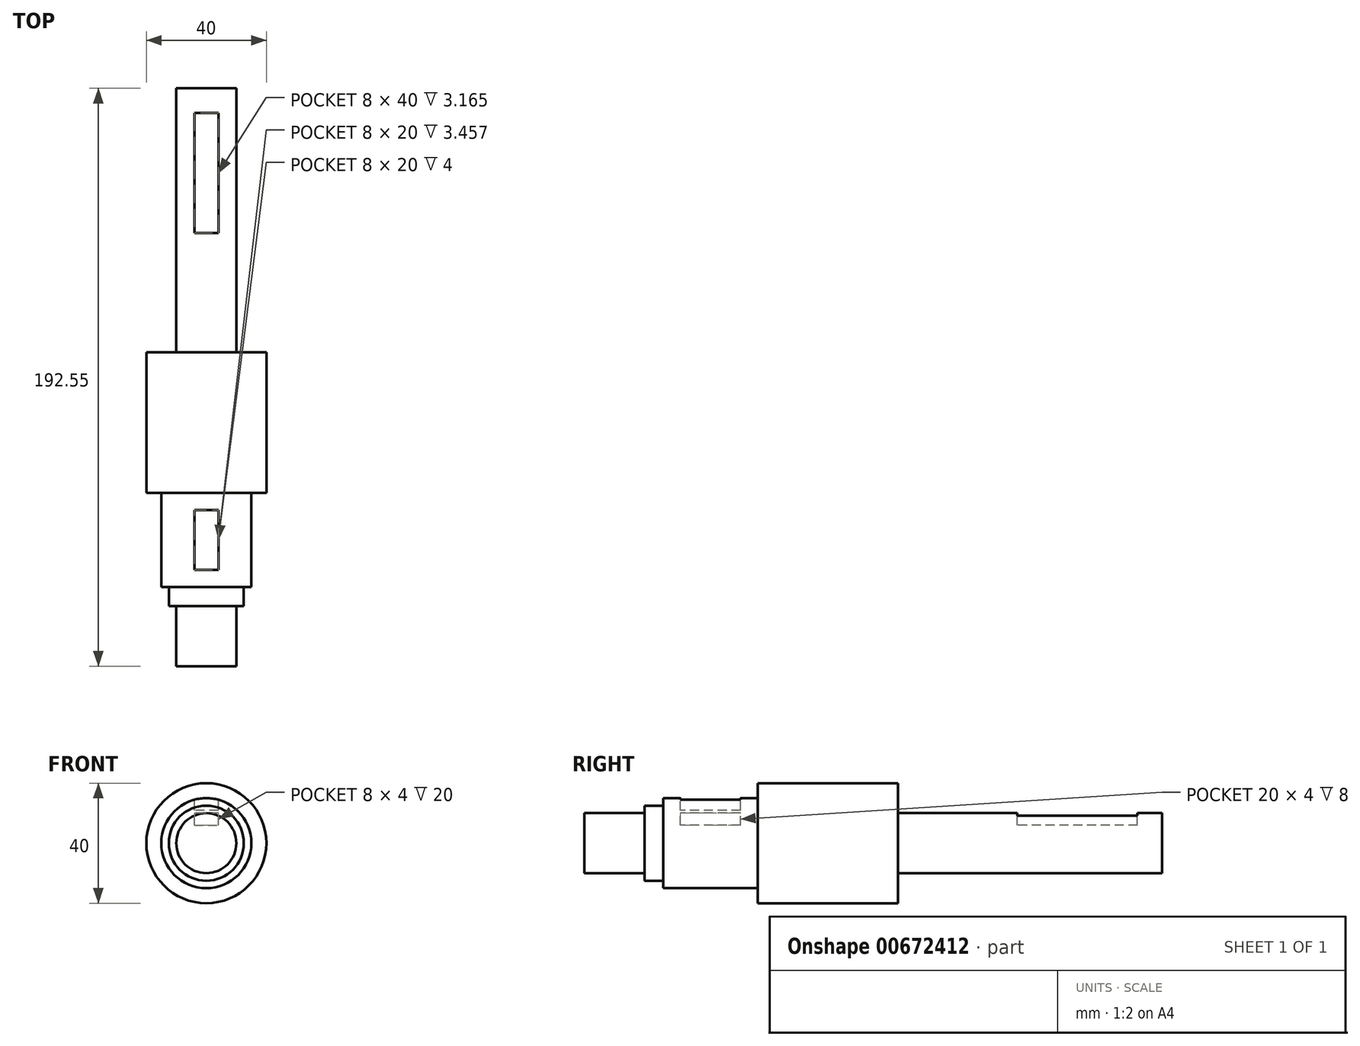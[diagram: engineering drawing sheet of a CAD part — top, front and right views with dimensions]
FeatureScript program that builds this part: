
annotation { "Feature Type Name" : "Feature", "Feature Type Description" : "" }
export const myFeature = defineFeature(function(context is Context, id is Id, definition is map)
    precondition{}
    {
        {
            var Q0;
            Q0=qCreatedBy(makeId("Front.planeOp"),FACE);
            var sketch = newSketch(context, id + "F0", { "sketchPlane" : qUnion([Q0])});
            skCircle(sketch, "E0", {"center": v(0, 0) * mm, "radius": 10 * mm});
            skSolve(sketch);
        }
        {
            var Q0;
            Q0 = qSketchRegion(id + "F0", true);
            extrude(context, id + "F1", {"entities" : qUnion([Q0]), "depth" : 88 * mm, "offsetDistance" : 25.4 * mm});
        }
        {
            var Q0;
            Q0=makeQuery(id+"F1.opExtrude","CAP_FACE",FACE,{"disambiguationData":[OSD([sQuery(id+"F0.wireOp",EDGE,"E0")])],"isStart":false});
            var sketch = newSketch(context, id + "F2", { "sketchPlane" : qUnion([Q0])});
            skCircle(sketch, "E1", {"center": v(0, 0) * mm, "radius": 20 * mm});
            skSolve(sketch);
        }
        {
            var Q0;
            Q0 = qSketchRegion(id + "F2", true);
            extrude(context, id + "F3", {"entities" : qUnion([Q0]), "operationType" : NewBodyOperationType.ADD, "depth" : 46.83 * mm, "offsetDistance" : 25.4 * mm});
        }
        {
            var Q0;
            Q0=makeQuery(id+"F3.opExtrude","CAP_FACE",FACE,{"disambiguationData":[OSD([sQuery(id+"F2.wireOp",EDGE,"E1")])],"isStart":false});
            var sketch = newSketch(context, id + "F4", { "sketchPlane" : qUnion([Q0])});
            skCircle(sketch, "E2", {"center": v(0, 0) * mm, "radius": 15 * mm});
            skSolve(sketch);
        }
        {
            var Q0;
            Q0 = qSketchRegion(id + "F4", true);
            extrude(context, id + "F5", {"entities" : qUnion([Q0]), "operationType" : NewBodyOperationType.ADD, "depth" : 25.4 * mm + 6 * mm, "offsetDistance" : 25.4 * mm});
        }
        {
            var Q0;
            Q0=makeQuery(id+"F5.opExtrude","CAP_FACE",FACE,{"disambiguationData":[OSD([sQuery(id+"F4.wireOp",EDGE,"E2")])],"isStart":false});
            var sketch = newSketch(context, id + "F6", { "sketchPlane" : qUnion([Q0])});
            skCircle(sketch, "E3", {"center": v(0, 0) * mm, "radius": 12.5 * mm});
            skSolve(sketch);
        }
        {
            var Q0;
            Q0 = qSketchRegion(id + "F6", true);
            extrude(context, id + "F7", {"entities" : qUnion([Q0]), "operationType" : NewBodyOperationType.ADD, "depth" : 19.32 * mm - 6 * mm - 7 * mm, "offsetDistance" : 25.4 * mm});
        }
        {
            var Q0;
            Q0=makeQuery(id+"F7.opExtrude","CAP_FACE",FACE,{"disambiguationData":[OSD([sQuery(id+"F6.wireOp",EDGE,"E3")])],"isStart":false});
            var sketch = newSketch(context, id + "F8", { "sketchPlane" : qUnion([Q0])});
            skCircle(sketch, "E4", {"center": v(0, 0) * mm, "radius": 10 * mm});
            skSolve(sketch);
        }
        {
            var Q0;
            Q0 = qSketchRegion(id + "F8", true);
            extrude(context, id + "F9", {"entities" : qUnion([Q0]), "operationType" : NewBodyOperationType.ADD, "depth" : 20 * mm, "offsetDistance" : 25.4 * mm});
        }
        {
            var Q0;
            Q0=qCreatedBy(makeId("Top.planeOp"),FACE);
            cPlane(context, id + "F10", {"entities" : qUnion([Q0]), "cplaneType" : CPlaneType.OFFSET, "offset" : 10 * mm, "width" : 152.4 * mm, "height" : 152.4 * mm});
        }
        {
            var Q0;
            Q0=qCreatedBy(id+"F10.planeOp",FACE);
            var sketch = newSketch(context, id + "F11", { "sketchPlane" : qUnion([Q0])});
            skLineSegment(sketch, "E5", {"start": v(0, 0) * mm, "end": v(0, -56.48) * mm});
            skLineSegment(sketch, "E6.bottom", {"start": v(-4, -8.24) * mm, "end": v(4, -8.24) * mm});
            skLineSegment(sketch, "E6.top", {"start": v(-4, -48.24) * mm, "end": v(4, -48.24) * mm});
            skLineSegment(sketch, "E6.left", {"start": v(-4, -8.24) * mm, "end": v(-4, -48.24) * mm});
            skLineSegment(sketch, "E6.right", {"start": v(4, -8.24) * mm, "end": v(4, -48.24) * mm});
            skPoint(sketch, "E6.middle", {"position": v(0, -28.24) * mm});
            skLineSegment(sketch, "E7.0", {"start": v(15, -166.23) * mm, "end": v(-15, -166.23) * mm});
            skLineSegment(sketch, "E8.0", {"start": v(20, -134.82) * mm, "end": v(-20, -134.82) * mm});
            skLineSegment(sketch, "E9", {"start": v(0, -166.23) * mm, "end": v(0, -134.82) * mm});
            skLineSegment(sketch, "E10.bottom", {"start": v(4, -140.53) * mm, "end": v(-4, -140.53) * mm});
            skLineSegment(sketch, "E10.top", {"start": v(4, -160.53) * mm, "end": v(-4, -160.53) * mm});
            skLineSegment(sketch, "E10.left", {"start": v(4, -140.53) * mm, "end": v(4, -160.53) * mm});
            skLineSegment(sketch, "E10.right", {"start": v(-4, -140.53) * mm, "end": v(-4, -160.53) * mm});
            skPoint(sketch, "E10.middle", {"position": v(0, -150.53) * mm});
            skSolve(sketch);
        }
        {
            var Q0;
            Q0 = qSketchRegion(id + "F11", true);
            extrude(context, id + "F12", {"entities" : qUnion([Q0]), "operationType" : NewBodyOperationType.REMOVE, "oppositeDirection" : true, "depth" : 4 * mm, "offsetDistance" : 25.4 * mm});
        }
        {
            var Q0;
            Q0=qCreatedBy(makeId("Top.planeOp"),FACE);
            cPlane(context, id + "F13", {"entities" : qUnion([Q0]), "cplaneType" : CPlaneType.OFFSET, "offset" : 15 * mm, "width" : 152.4 * mm, "height" : 152.4 * mm});
        }
        {
            var Q0;
            Q0=qCreatedBy(id+"F13.planeOp",FACE);
            var sketch = newSketch(context, id + "F14", { "sketchPlane" : qUnion([Q0])});
            skLineSegment(sketch, "E11.0", {"start": v(20, -134.82) * mm, "end": v(-20, -134.82) * mm});
            skLineSegment(sketch, "E12.0", {"start": v(15, -166.23) * mm, "end": v(-15, -166.23) * mm});
            skLineSegment(sketch, "E13", {"start": v(0, -166.23) * mm, "end": v(0, -134.82) * mm});
            skLineSegment(sketch, "E14.bottom", {"start": v(4, -140.53) * mm, "end": v(-4, -140.53) * mm});
            skLineSegment(sketch, "E14.top", {"start": v(4, -160.53) * mm, "end": v(-4, -160.53) * mm});
            skLineSegment(sketch, "E14.left", {"start": v(4, -140.53) * mm, "end": v(4, -160.53) * mm});
            skLineSegment(sketch, "E14.right", {"start": v(-4, -140.53) * mm, "end": v(-4, -160.53) * mm});
            skPoint(sketch, "E14.middle", {"position": v(0, -150.53) * mm});
            skSolve(sketch);
        }
        {
            var Q0;
            Q0 = qSketchRegion(id + "F14", true);
            extrude(context, id + "F15", {"entities" : qUnion([Q0]), "operationType" : NewBodyOperationType.REMOVE, "oppositeDirection" : true, "depth" : 4 * mm, "offsetDistance" : 25.4 * mm});
        }
    });
